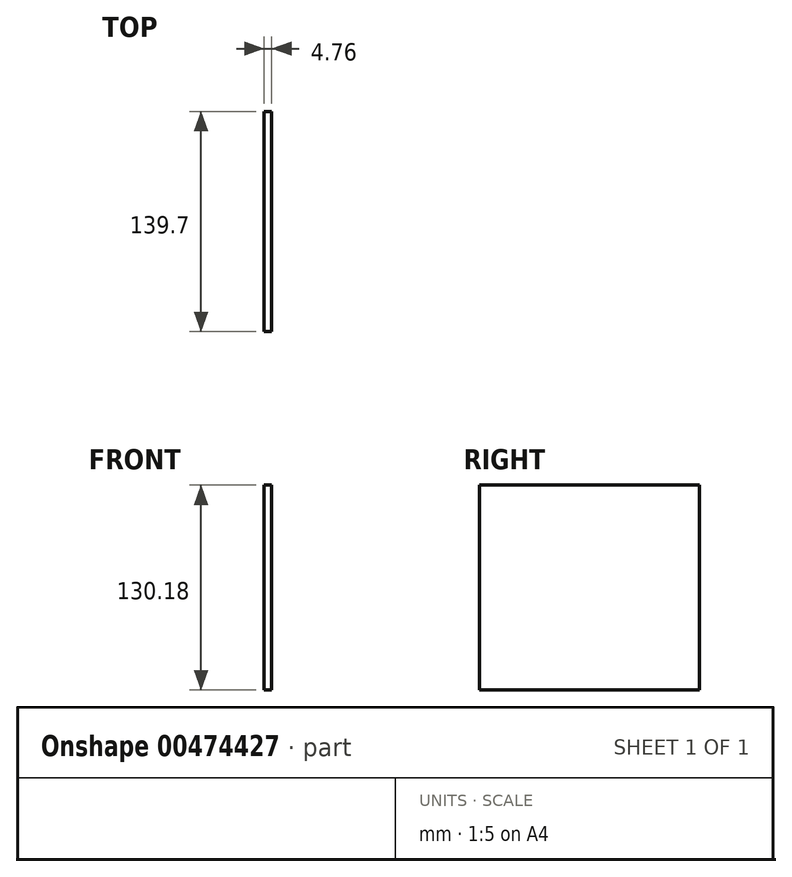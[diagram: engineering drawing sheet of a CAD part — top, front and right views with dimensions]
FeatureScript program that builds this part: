
annotation { "Feature Type Name" : "Feature", "Feature Type Description" : "" }
export const myFeature = defineFeature(function(context is Context, id is Id, definition is map)
    precondition{}
    {
        {
            var Q0;
            Q0=qCreatedBy(makeId("Right.planeOp"),FACE);
            var sketch = newSketch(context, id + "F0", { "sketchPlane" : qUnion([Q0])});
            skLineSegment(sketch, "E0.bottom", {"start": v(-69.85, -65.09) * mm, "end": v(69.85, -65.09) * mm});
            skLineSegment(sketch, "E0.top", {"start": v(-69.85, 65.09) * mm, "end": v(69.85, 65.09) * mm});
            skLineSegment(sketch, "E0.left", {"start": v(-69.85, -65.09) * mm, "end": v(-69.85, 65.09) * mm});
            skLineSegment(sketch, "E0.right", {"start": v(69.85, -65.09) * mm, "end": v(69.85, 65.09) * mm});
            skPoint(sketch, "E0.middle", {"position": v(0, 0) * mm});
            skSolve(sketch);
        }
        {
            var Q0;
            Q0=qSketchRegion(id+"F0",true);
            extrude(context, id + "F1", {"entities" : qUnion([Q0]), "depth" : 4.76 * mm});
        }
    });
